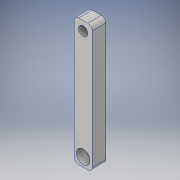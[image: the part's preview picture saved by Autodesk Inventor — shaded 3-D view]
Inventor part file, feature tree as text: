
AUTODESK INVENTOR PART (.ipt)
format: ipt  version: 2016 (Build 200138000, 138)  size: 128,512 bytes
history: native  units: in
note: dims shown in document units (in); Inventor stores cm internally (conversion verified against a paired STEP export)
features: sketch x4, extrude x2, hole x1, plane x1, mirror x1, fillet x1
ambient origin geometry x8: Origin, YZ Plane, XZ Plane, XY Plane, X Axis, Y Axis, Z Axis, Center Point
bodies: Body1 (feature_tree)
feature tree (10):
  extrude  "Extrusion3"  Depth=0.5in
  hole  "Hole1"  [1 undecoded]
  sketch  "Sketch5"  dims[d15=0.257in d16=0.75in d17=0.375in d18=0.25in d19=0.5635in d20=1.0in d21=0.8108in d22=0.25in]
  plane  "Work Plane1"
  mirror  "Mirror1"
  fillet  "Fillet1"  Radius=0.25in
  extrude  "Extrusion4"  Depth=0.25in
  sketch  "Sketch1"  dims[d6=3.5in d7=0.5in]
  sketch  "Sketch4"  dims[d8=0.375in d9=0.0in d13=0.25in d14=0.25in]
  sketch  "Sketch6"  dims[d23=90.0deg d24=0.125in d25=0.375in d26=0.25in d27=0.0in]
note: 1 required parameter value undecoded (feature->parameter linkage not recoverable at this tier; creation-order binding heuristic only, values carry confidence <= 0.55)
